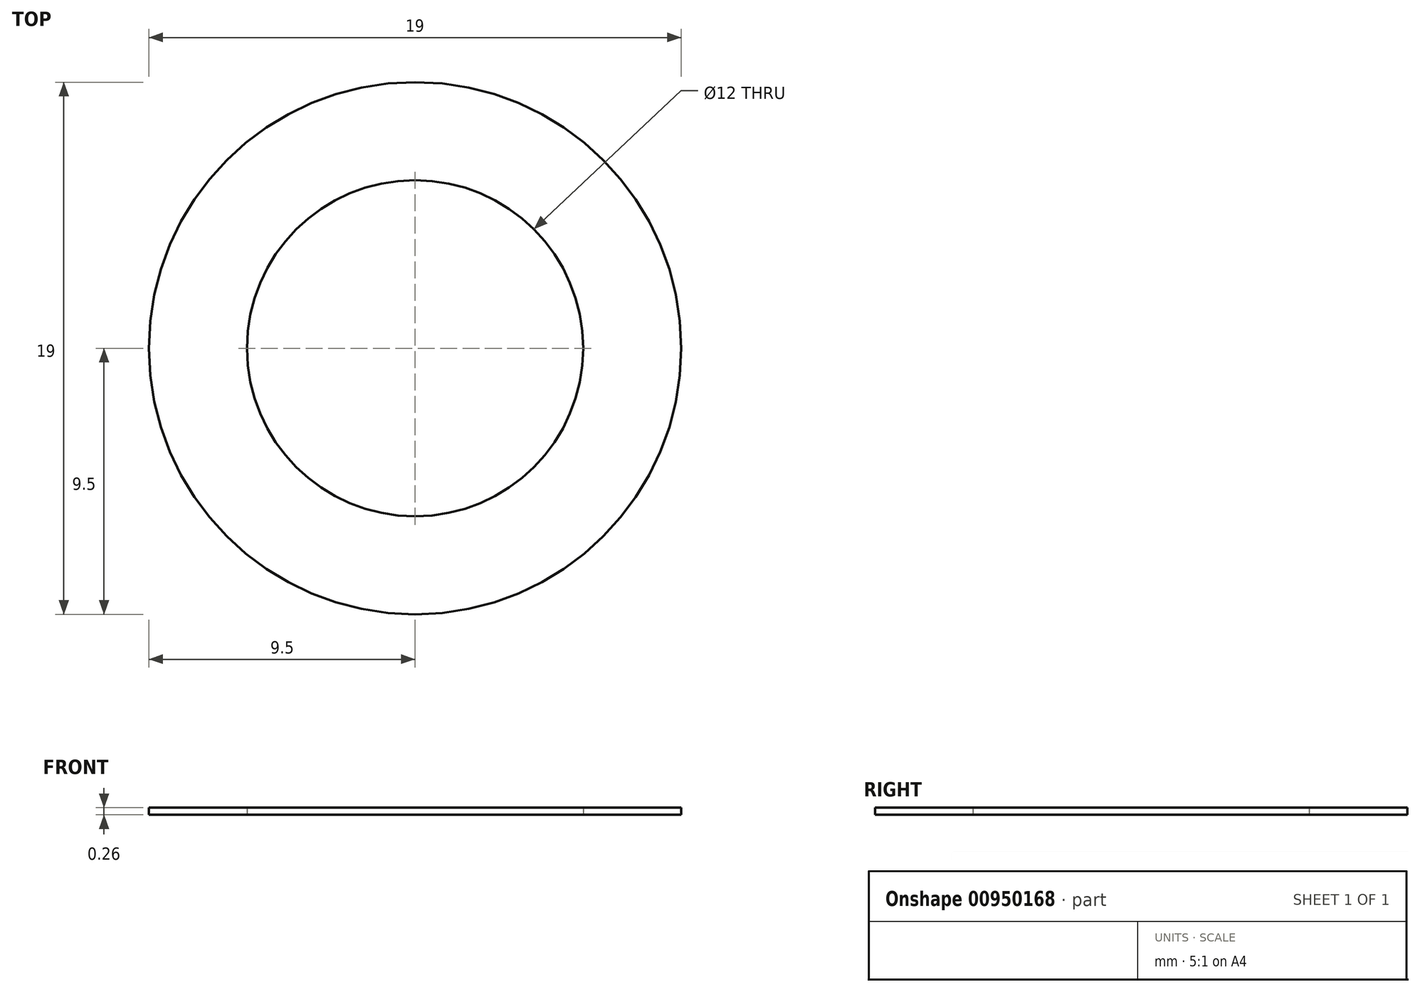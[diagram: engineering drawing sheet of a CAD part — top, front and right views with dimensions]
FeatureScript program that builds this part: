
annotation { "Feature Type Name" : "Feature", "Feature Type Description" : "" }
export const myFeature = defineFeature(function(context is Context, id is Id, definition is map)
    precondition{}
    {
        {
            var Q0;
            Q0=qCreatedBy(makeId("Top.planeOp"),FACE);
            var sketch = newSketch(context, id + "F0", { "sketchPlane" : qUnion([Q0])});
            skCircle(sketch, "E0", {"center": v(0, 0) * mm, "radius": 6 * mm});
            skCircle(sketch, "E1", {"center": v(0, 0) * mm, "radius": 9.5 * mm});
            skSolve(sketch);
        }
        {
            var Q0;
            Q0 = qSketchRegion(id + "F0", true);
            extrude(context, id + "F1", {"entities" : qUnion([Q0]), "depth" : 0.26 * mm, "offsetDistance" : 25.4 * mm});
        }
    });
